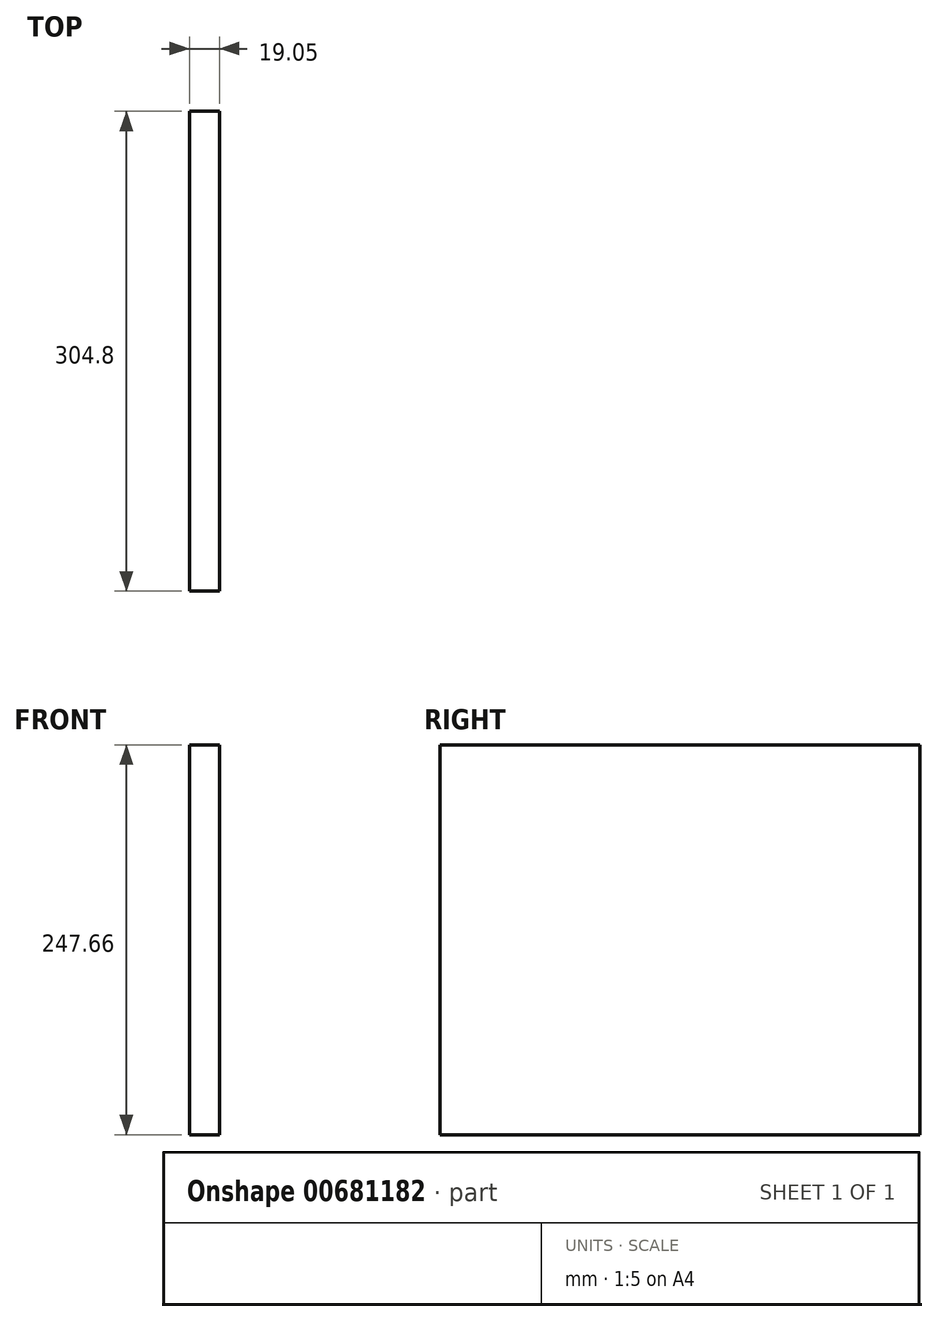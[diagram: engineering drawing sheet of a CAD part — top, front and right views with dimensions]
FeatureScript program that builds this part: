
annotation { "Feature Type Name" : "Feature", "Feature Type Description" : "" }
export const myFeature = defineFeature(function(context is Context, id is Id, definition is map)
    precondition{}
    {
        {
            var Q0;
            Q0=qCreatedBy(makeId("Right.planeOp"),FACE);
            var sketch = newSketch(context, id + "F0", { "sketchPlane" : qUnion([Q0])});
            skLineSegment(sketch, "E0.bottom", {"start": v(152.4, 123.83) * mm, "end": v(-152.4, 123.83) * mm});
            skLineSegment(sketch, "E0.top", {"start": v(152.4, -123.83) * mm, "end": v(-152.4, -123.83) * mm});
            skLineSegment(sketch, "E0.left", {"start": v(152.4, 123.83) * mm, "end": v(152.4, -123.83) * mm});
            skLineSegment(sketch, "E0.right", {"start": v(-152.4, 123.83) * mm, "end": v(-152.4, -123.83) * mm});
            skPoint(sketch, "E0.middle", {"position": v(0, 0) * mm});
            skSolve(sketch);
        }
        {
            var Q0;
            Q0=makeQuery(id+"F0.imprint","IMPRINT",FACE,{"disambiguationData":[TD([[makeQuery(id+"F0.imprint","IMPRINT",EDGE,{"derivedFrom":sQuery(id+"F0.wireOp",EDGE,"E0.bottom")}),1.0]])]});
            extrude(context, id + "F1", {"entities" : qUnion([Q0]), "depth" : 19.05 * mm, "offsetDistance" : 25.4 * mm});
        }
    });
